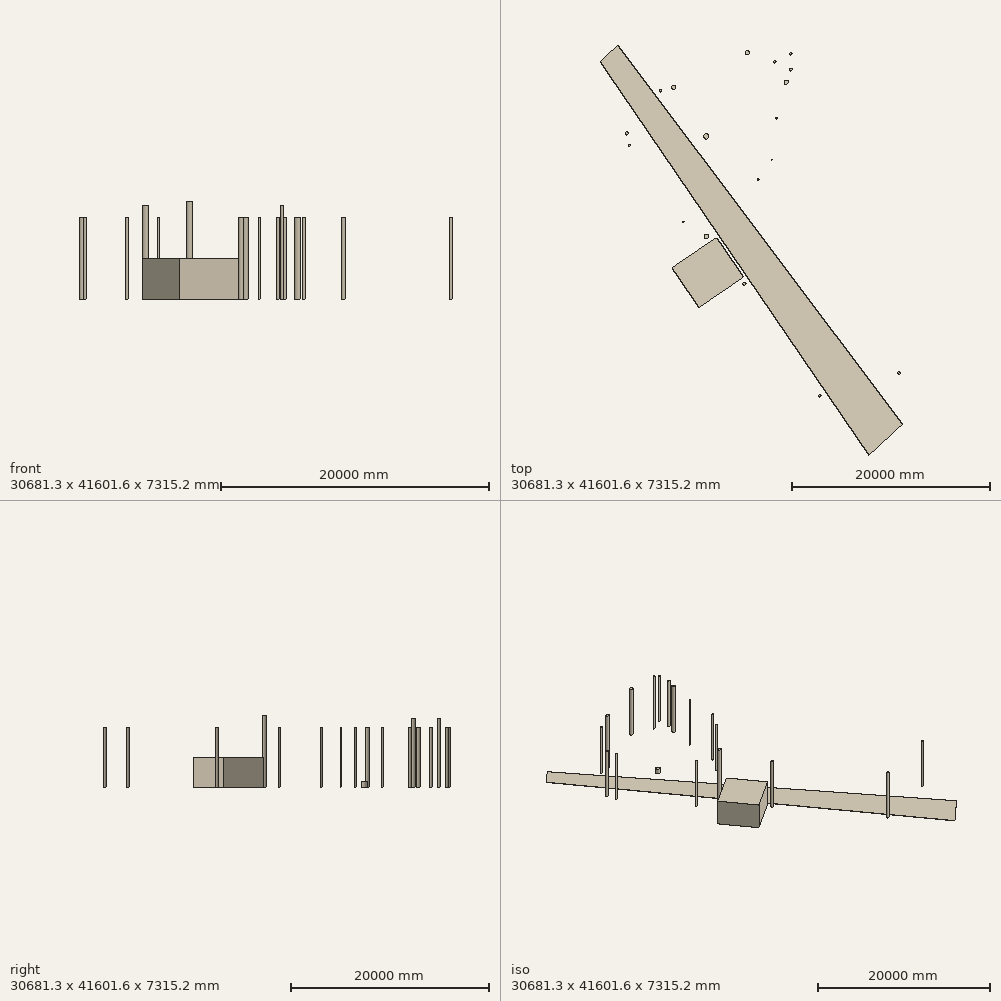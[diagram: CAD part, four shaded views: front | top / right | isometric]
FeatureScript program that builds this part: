
annotation { "Feature Type Name" : "Feature", "Feature Type Description" : "" }
export const myFeature = defineFeature(function(context is Context, id is Id, definition is map)
    precondition{}
    {
        {
            var Q0;
            Q0=qCreatedBy(makeId("Top.planeOp"),FACE);
            var sketch = newSketch(context, id + "F0", { "sketchPlane" : qUnion([Q0])});
            skCircle(sketch, "E0", {"center": v(0, 0) * mm, "radius": 266.8 * mm});
            skCircle(sketch, "E1", {"center": v(0, -10149.33) * mm, "radius": 230.42 * mm});
            skLineSegment(sketch, "E2", {"start": v(-2918.77, 1852.42) * mm, "end": v(-4383.13, 1852.42) * mm});
            skLineSegment(sketch, "E3", {"start": v(-4383.13, 1852.42) * mm, "end": v(-3923.73, 2153.91) * mm});
            skLineSegment(sketch, "E4", {"start": v(-3923.73, 2153.91) * mm, "end": v(-3923.73, 1436.09) * mm});
            skLineSegment(sketch, "E5", {"start": v(-3923.73, 1436.09) * mm, "end": v(-4383.13, 1852.42) * mm});
            skSolve(sketch);
        }
        {
            var Q0;
            Q0=makeQuery(id+"F0.imprint","IMPRINT",FACE,{"disambiguationData":[TD([[makeQuery(id+"F0.imprint","IMPRINT",EDGE,{"derivedFrom":sQuery(id+"F0.wireOp",EDGE,"E0")}),1.0]])]});
            extrude(context, id + "F1", {"entities" : qUnion([Q0]), "depth" : 609.6 * mm});
        }
        {
            var Q0;
            Q0=makeQuery(id+"F0.imprint","IMPRINT",FACE,{"disambiguationData":[TD([[makeQuery(id+"F0.imprint","IMPRINT",EDGE,{"derivedFrom":sQuery(id+"F0.wireOp",EDGE,"E1")}),1.0]])]});
            extrude(context, id + "F2", {"entities" : qUnion([Q0]), "depth" : 7315.2 * mm});
        }
        {
            var Q0;
            Q0=qCreatedBy(makeId("Top.planeOp"),FACE);
            var sketch = newSketch(context, id + "F3", { "sketchPlane" : qUnion([Q0])});
            skCircle(sketch, "E6.0", {"center": v(0, 0) * mm, "radius": 266.8 * mm, "construction": true});
            skCircle(sketch, "E7.0", {"center": v(0, -10149.33) * mm, "radius": 230.42 * mm, "construction": true});
            skCircle(sketch, "E8", {"center": v(-8050.48, 313.82) * mm, "radius": 169.79 * mm});
            skCircle(sketch, "E9", {"center": v(-7789.03, -923.2) * mm, "radius": 109.15 * mm});
            skCircle(sketch, "E10", {"center": v(-2321.42, -8660.62) * mm, "radius": 88.94 * mm});
            skCircle(sketch, "E11", {"center": v(3871.27, -14981.19) * mm, "radius": 169.79 * mm});
            skCircle(sketch, "E12", {"center": v(-4651.68, 4625.92) * mm, "radius": 121.28 * mm});
            skCircle(sketch, "E13", {"center": v(4177.03, 8506.49) * mm, "radius": 218.3 * mm});
            skCircle(sketch, "E14", {"center": v(8582, 8362.56) * mm, "radius": 133.4 * mm});
            skCircle(sketch, "E15", {"center": v(8579.72, 6768.17) * mm, "radius": 145.53 * mm});
            skCircle(sketch, "E16", {"center": v(8102.8, 5493.74) * mm, "radius": 226.4 * mm});
            skCircle(sketch, "E17", {"center": v(7147.05, 1864.93) * mm, "radius": 109.15 * mm});
            skCircle(sketch, "E18", {"center": v(6648.12, -2380.13) * mm, "radius": 88.94 * mm});
            skCircle(sketch, "E19", {"center": v(5249.21, -4386.65) * mm, "radius": 97.02 * mm});
            skCircle(sketch, "E20", {"center": v(11530.66, -26332.7) * mm, "radius": 133.4 * mm});
            skCircle(sketch, "E21", {"center": v(19569.1, -24019.08) * mm, "radius": 133.4 * mm});
            skSolve(sketch);
        }
        {
            var Q0;
            Q0 = qSketchRegion(id + "F3", true);
            extrude(context, id + "F4", {"entities" : qUnion([Q0]), "depth" : 6096 * mm});
        }
        {
            var Q0;
            Q0=qCreatedBy(makeId("Top.planeOp"),FACE);
            var sketch = newSketch(context, id + "F5", { "sketchPlane" : qUnion([Q0])});
            skCircle(sketch, "E22.0", {"center": v(0, 0) * mm, "radius": 266.8 * mm, "construction": true});
            skCircle(sketch, "E23.0", {"center": v(0, -10149.33) * mm, "radius": 230.42 * mm, "construction": true});
            skCircle(sketch, "E24", {"center": v(-3288.8, 4974.53) * mm, "radius": 210.2 * mm});
            skCircle(sketch, "E25", {"center": v(6967.73, 7572.03) * mm, "radius": 117.23 * mm});
            skSolve(sketch);
        }
        {
            var Q0;
            Q0 = qSketchRegion(id + "F5", true);
            extrude(context, id + "F6", {"entities" : qUnion([Q0]), "depth" : 7010.4 * mm});
        }
        {
            var Q0;
            Q0=qCreatedBy(makeId("Top.planeOp"),FACE);
            var sketch = newSketch(context, id + "F7", { "sketchPlane" : qUnion([Q0])});
            skPoint(sketch, "E26.0", {"position": v(-8050.48, 313.82) * mm});
            skPoint(sketch, "E27.0", {"position": v(0, 0) * mm});
            skPoint(sketch, "E28.0", {"position": v(0, -10149.33) * mm});
            skLineSegment(sketch, "E29", {"start": v(-8050.48, 313.82) * mm, "end": v(0, 0) * mm, "construction": true});
            skLineSegment(sketch, "E30", {"start": v(0, -10149.33) * mm, "end": v(0, 0) * mm, "construction": true});
            skCircle(sketch, "E31.0", {"center": v(0, 0) * mm, "radius": 266.8 * mm, "construction": true});
            skPoint(sketch, "E32", {"position": v(-5748.84, 224.1) * mm});
            skPoint(sketch, "E33", {"position": v(-2094.02, 81.63) * mm});
            skPoint(sketch, "E34", {"position": v(0, -8191.6) * mm});
            skPoint(sketch, "E35", {"position": v(0, -2705.2) * mm});
            skLineSegment(sketch, "E36", {"start": v(-10761.85, 7562.62) * mm, "end": v(16515.5, -32368.57) * mm});
            skLineSegment(sketch, "E37", {"start": v(-8970.3, 9232.98) * mm, "end": v(19919.45, -29215.13) * mm});
            skLineSegment(sketch, "E38", {"start": v(-10761.85, 7562.62) * mm, "end": v(-8970.3, 9232.98) * mm});
            skLineSegment(sketch, "E39", {"start": v(19919.45, -29215.13) * mm, "end": v(16515.5, -32368.57) * mm});
            skSolve(sketch);
        }
        {
            var Q0;
            Q0 = qSketchRegion(id + "F7", true);
            extrude(context, id + "F8", {"entities" : qUnion([Q0]), "depth" : 25.4 * mm});
        }
        {
            var Q0;
            Q0=qCreatedBy(makeId("Top.planeOp"),FACE);
            var sketch = newSketch(context, id + "F9", { "sketchPlane" : qUnion([Q0])});
            skCircle(sketch, "E40.0", {"center": v(0, -10149.33) * mm, "radius": 230.42 * mm, "construction": true});
            skLineSegment(sketch, "E41.0", {"start": v(-10761.85, 7562.62) * mm, "end": v(16515.5, -32368.57) * mm, "construction": true});
            skCircle(sketch, "E42.0", {"center": v(3871.27, -14981.19) * mm, "radius": 169.79 * mm, "construction": true});
            skLineSegment(sketch, "E43", {"start": v(1042.96, -10258.75) * mm, "end": v(3793.79, -14285.68) * mm});
            skLineSegment(sketch, "E44", {"start": v(3793.79, -14285.68) * mm, "end": v(-736.5, -17380.36) * mm});
            skLineSegment(sketch, "E45", {"start": v(-736.5, -17380.36) * mm, "end": v(-3487.33, -13353.44) * mm});
            skLineSegment(sketch, "E46", {"start": v(-3487.33, -13353.44) * mm, "end": v(1042.96, -10258.75) * mm});
            skLineSegment(sketch, "E47", {"start": v(382.8, -10709.71) * mm, "end": v(129.97, -10339.6) * mm, "construction": true});
            skLineSegment(sketch, "E48", {"start": v(3522.67, -14470.88) * mm, "end": v(3775.5, -14841) * mm, "construction": true});
            skSolve(sketch);
        }
        {
            var Q0;
            Q0=makeQuery(id+"F9.imprint","IMPRINT",FACE,{"disambiguationData":[TD([[makeQuery(id+"F9.imprint","IMPRINT",EDGE,{"derivedFrom":sQuery(id+"F9.wireOp",EDGE,"E43")}),-1.0]])]});
            extrude(context, id + "F10", {"entities" : qUnion([Q0]), "depth" : 3048 * mm});
        }
    });
